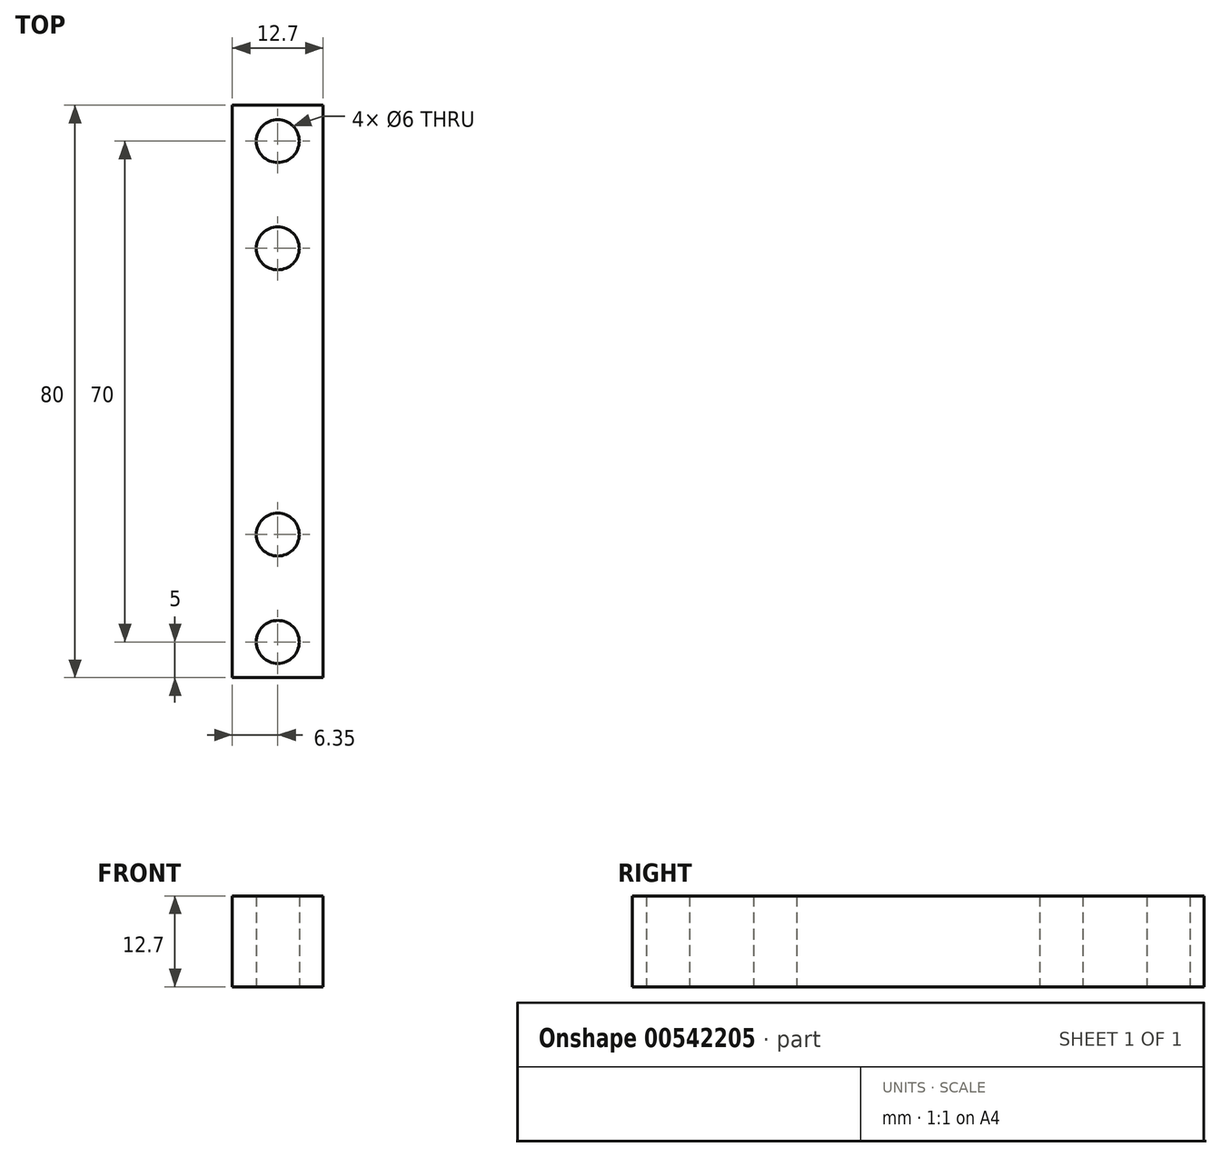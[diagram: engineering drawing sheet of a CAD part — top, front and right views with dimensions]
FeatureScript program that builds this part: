
annotation { "Feature Type Name" : "Feature", "Feature Type Description" : "" }
export const myFeature = defineFeature(function(context is Context, id is Id, definition is map)
    precondition{}
    {
        {
            var Q0;
            Q0=qCreatedBy(makeId("Top.planeOp"),FACE);
            var sketch = newSketch(context, id + "F0", { "sketchPlane" : qUnion([Q0])});
            skLineSegment(sketch, "E0.bottom", {"start": v(6.35, 40) * mm, "end": v(-6.35, 40) * mm});
            skLineSegment(sketch, "E0.top", {"start": v(6.35, -40) * mm, "end": v(-6.35, -40) * mm});
            skLineSegment(sketch, "E0.left", {"start": v(6.35, 40) * mm, "end": v(6.35, -40) * mm});
            skLineSegment(sketch, "E0.right", {"start": v(-6.35, 40) * mm, "end": v(-6.35, -40) * mm});
            skPoint(sketch, "E0.middle", {"position": v(0, 0) * mm});
            skCircle(sketch, "E1", {"center": v(0, -35) * mm, "radius": 3 * mm});
            skCircle(sketch, "E2", {"center": v(0, -20) * mm, "radius": 3 * mm});
            skCircle(sketch, "E3", {"center": v(0, 35) * mm, "radius": 3 * mm});
            skCircle(sketch, "E4", {"center": v(0, 20) * mm, "radius": 3 * mm});
            skSolve(sketch);
        }
        {
            var Q0;
            Q0=makeQuery(id+"F0.imprint","IMPRINT",FACE,{"disambiguationData":[TD([[makeQuery(id+"F0.imprint","IMPRINT",EDGE,{"derivedFrom":sQuery(id+"F0.wireOp",EDGE,"E0.bottom")}),1.0]])]});
            extrude(context, id + "F1", {"entities" : qUnion([Q0]), "depth" : 12.7 * mm, "offsetDistance" : 25 * mm});
        }
    });
